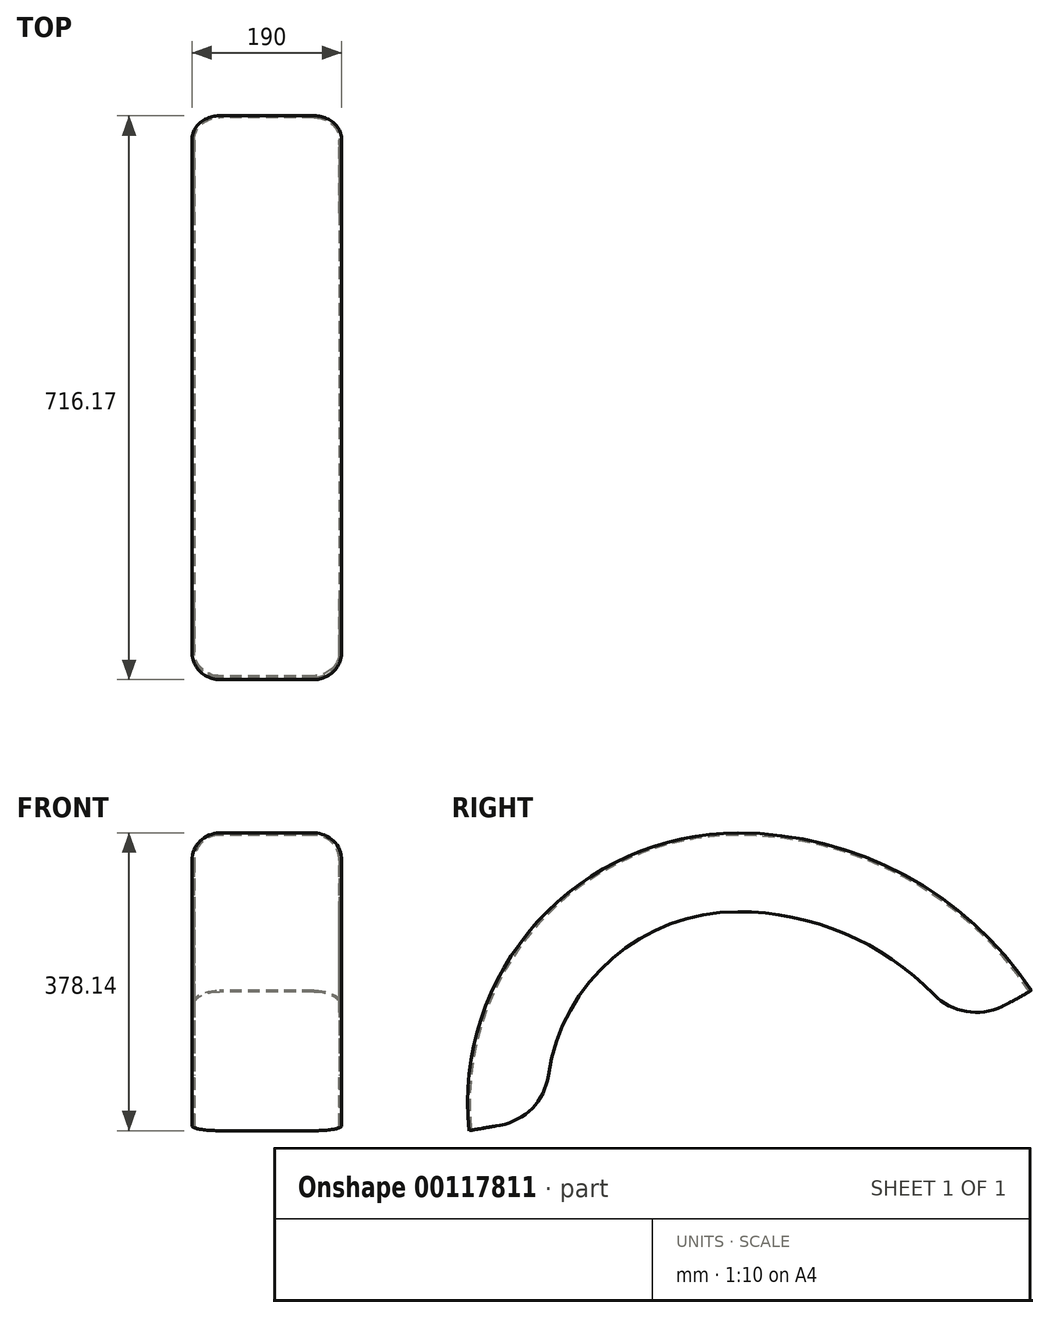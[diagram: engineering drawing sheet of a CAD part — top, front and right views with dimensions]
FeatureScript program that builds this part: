
annotation { "Feature Type Name" : "Feature", "Feature Type Description" : "" }
export const myFeature = defineFeature(function(context is Context, id is Id, definition is map)
    precondition{}
    {
        {
            var Q0;
            Q0=qCreatedBy(makeId("Right.planeOp"),FACE);
            var sketch = newSketch(context, id + "F0", { "sketchPlane" : qUnion([Q0])});
            skArc(sketch, "E0", {"start": v(1154.6, 411) * mm, "mid": v(1241.29, 675.93) * mm, "end": v(1496.02, 789.14) * mm});
            skLineSegment(sketch, "E1.trimOffspring", {"start": v(1833.99, 505.65) * mm, "end": v(1735.51, 488.25) * mm, "construction": true});
            skLineSegment(sketch, "E2", {"start": v(1154.6, 411) * mm, "end": v(1253.45, 428.47) * mm});
            skArc(sketch, "E3", {"start": v(1735.51, 488.25) * mm, "mid": v(1652.31, 632.27) * mm, "end": v(1496.02, 689.14) * mm, "construction": true});
            skLineSegment(sketch, "E4", {"start": v(1808.2, 362.29) * mm, "end": v(1929.78, 815.99) * mm, "construction": true});
            skLineSegment(sketch, "E5", {"start": v(1496.02, 445.94) * mm, "end": v(1033.19, 364.16) * mm, "construction": true});
            skLineSegment(sketch, "E6", {"start": v(1496.02, 445.94) * mm, "end": v(1496.02, 789.14) * mm, "construction": true});
            skArc(sketch, "E7", {"start": v(1496.02, 789.14) * mm, "mid": v(1707.63, 735.98) * mm, "end": v(1869, 589.14) * mm});
            skPoint(sketch, "E8", {"position": v(1869, 589.14) * mm});
            skArc(sketch, "E9", {"start": v(1496.02, 789.14) * mm, "mid": v(1716.58, 708.88) * mm, "end": v(1833.99, 505.65) * mm, "construction": true});
            skArc(sketch, "E10", {"start": v(1496.02, 689.14) * mm, "mid": v(1653.82, 651.28) * mm, "end": v(1777.26, 545.94) * mm});
            skArc(sketch, "E11", {"start": v(1496.02, 689.14) * mm, "mid": v(1317.98, 611.62) * mm, "end": v(1253.45, 428.47) * mm});
            skArc(sketch, "E12", {"start": v(1777.26, 545.94) * mm, "mid": v(1824.22, 565.2) * mm, "end": v(1869, 589.14) * mm});
            skLineSegment(sketch, "E13", {"start": v(1496.02, 445.94) * mm, "end": v(1413.94, 910.49) * mm, "construction": true});
            skCircle(sketch, "E14", {"center": v(1496.02, 445.94) * mm, "radius": 323.2 * mm, "construction": true});
            skSolve(sketch);
        }
        {
            var Q0;
            Q0 = qSketchRegion(id + "F0", true);
            extrude(context, id + "F1", {"entities" : qUnion([Q0]), "endBound" : BoundingType.SYMMETRIC, "depth" : 190 * mm});
        }
        {
            var Q0;
            Q0=makeQuery(id+"F1.opExtrude","CAP_EDGE",EDGE,{"disambiguationData":[OSD([sQuery(id+"F0.wireOp",EDGE,"E0")])],"isStart":false});
            var Q1;
            Q1=makeQuery(id+"F1.opExtrude","CAP_EDGE",EDGE,{"disambiguationData":[OSD([sQuery(id+"F0.wireOp",EDGE,"E0")])],"isStart":true});
            fillet(context, id + "F2", {"entities" : qUnion([Q0, Q1]), "radius" : 35 * mm, "tangentPropagation" : true, "allowEdgeOverflow" : false});
        }
        {
            var Q0;
            Q0=makeQuery(id+"F1.opExtrude","SWEPT_EDGE",EDGE,{"disambiguationData":[OSD([sQuery(id+"F0.wireOp",EDGE,"E10"),sQuery(id+"F0.wireOp",EDGE,"E12")])]});
            var Q1;
            Q1=makeQuery(id+"F1.opExtrude","SWEPT_EDGE",EDGE,{"disambiguationData":[OSD([sQuery(id+"F0.wireOp",EDGE,"E2"),sQuery(id+"F0.wireOp",EDGE,"E11")])]});
            fillet(context, id + "F3", {"entities" : qUnion([Q0, Q1]), "radius" : 75 * mm, "tangentPropagation" : true, "allowEdgeOverflow" : false});
        }
        {
            var Q0;
            Q0=makeQuery(id+"F1.opExtrude","SWEPT_FACE",FACE,{"disambiguationData":[OSD([sQuery(id+"F0.wireOp",EDGE,"E3")])]});
            var Q1;
            Q1=makeQuery(id+"F3.opFillet","BLEND_FACE",FACE,{"disambiguationData":[OSD([sQuery(id+"F0.wireOp",EDGE,"E1.trimOffspring"),sQuery(id+"F0.wireOp",EDGE,"E3")])]});
            var Q2;
            Q2=makeQuery(id+"F1.opExtrude","SWEPT_FACE",FACE,{"disambiguationData":[OSD([sQuery(id+"F0.wireOp",EDGE,"E2")])]});
            var Q3;
            Q3=makeQuery(id+"F1.opExtrude","SWEPT_FACE",FACE,{"disambiguationData":[OSD([sQuery(id+"F0.wireOp",EDGE,"E1.trimOffspring")])]});
            var Q4;
            Q4=makeQuery(id+"F1.opExtrude","SWEPT_FACE",FACE,{"disambiguationData":[OSD([sQuery(id+"F0.wireOp",EDGE,"E11")])]});
            var Q5;
            Q5=makeQuery(id+"F1.opExtrude","SWEPT_FACE",FACE,{"disambiguationData":[OSD([sQuery(id+"F0.wireOp",EDGE,"E10")])]});
            var Q6;
            Q6=makeQuery(id+"F1.opExtrude","SWEPT_FACE",FACE,{"disambiguationData":[OSD([sQuery(id+"F0.wireOp",EDGE,"E12")])]});
            var Q7;
            Q7=makeQuery(id+"F3.opFillet","BLEND_FACE",FACE,{"disambiguationData":[OSD([sQuery(id+"F0.wireOp",EDGE,"E10"),sQuery(id+"F0.wireOp",EDGE,"E12")])]});
            var Q8;
            Q8=makeQuery(id+"F3.opFillet","BLEND_FACE",FACE,{"disambiguationData":[OSD([sQuery(id+"F0.wireOp",EDGE,"E2"),sQuery(id+"F0.wireOp",EDGE,"E11")])]});
            shell(context, id + "F4", {"entities" : qUnion([Q0, Q1, Q2, Q3, Q4, Q5, Q6, Q7, Q8]), "thickness" : 3 * mm});
        }
    });
